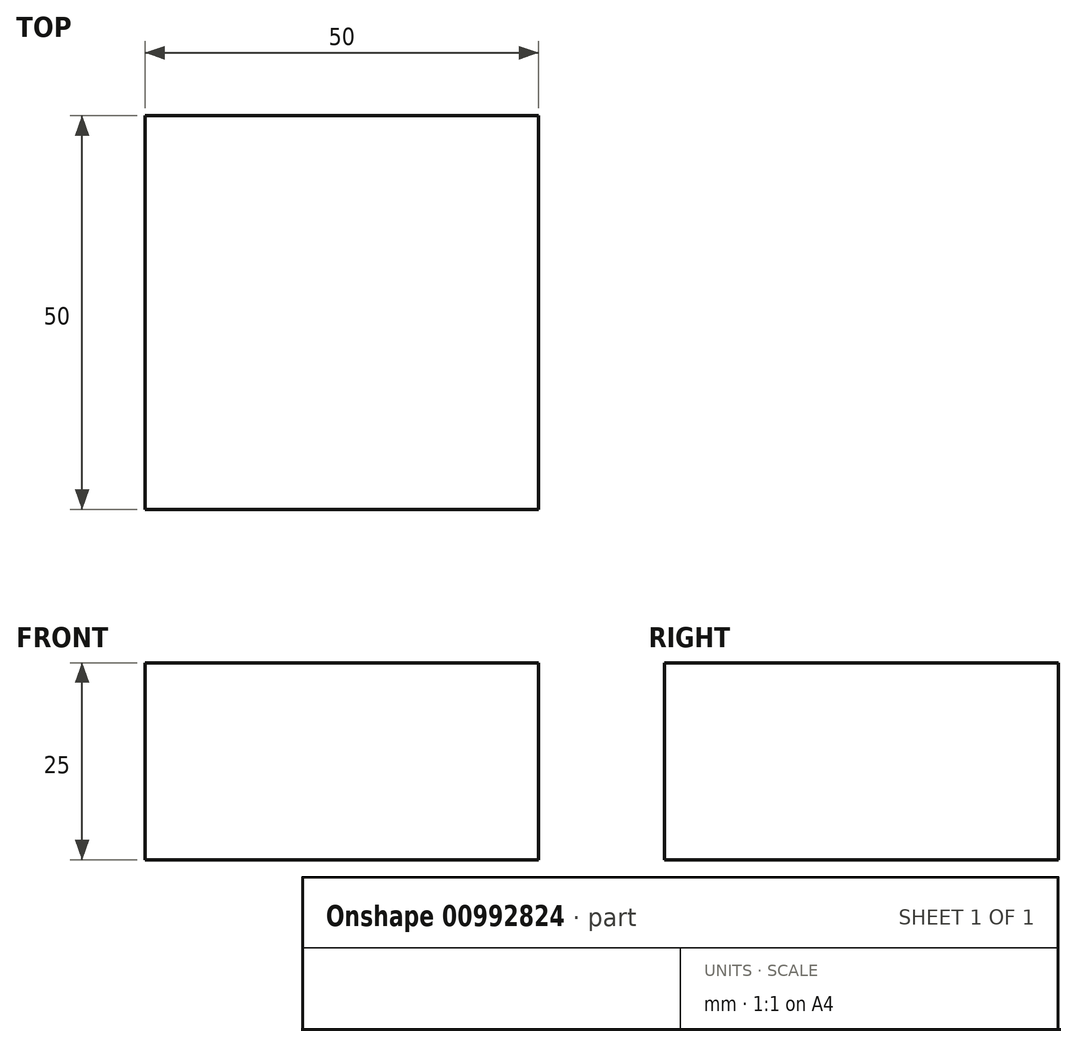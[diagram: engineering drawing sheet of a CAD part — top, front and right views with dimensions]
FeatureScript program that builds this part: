
annotation { "Feature Type Name" : "Feature", "Feature Type Description" : "" }
export const myFeature = defineFeature(function(context is Context, id is Id, definition is map)
    precondition{}
    {
        {
            var Q0;
            Q0=qCreatedBy(makeId("Top.planeOp"),FACE);
            var sketch = newSketch(context, id + "F0", { "sketchPlane" : qUnion([Q0])});
            skLineSegment(sketch, "E0.bottom", {"start": v(-31.6, 37.18) * mm, "end": v(18.4, 37.18) * mm});
            skLineSegment(sketch, "E0.top", {"start": v(-31.6, -12.82) * mm, "end": v(18.4, -12.82) * mm});
            skLineSegment(sketch, "E0.left", {"start": v(-31.6, 37.18) * mm, "end": v(-31.6, -12.82) * mm});
            skLineSegment(sketch, "E0.right", {"start": v(18.4, 37.18) * mm, "end": v(18.4, -12.82) * mm});
            skSolve(sketch);
        }
        {
            var Q0;
            Q0=makeQuery(id+"F0.imprint","IMPRINT",FACE,{"disambiguationData":[TD([[makeQuery(id+"F0.imprint","IMPRINT",EDGE,{"derivedFrom":sQuery(id+"F0.wireOp",EDGE,"E0.bottom")}),-1.0]])]});
            extrude(context, id + "F1", {"entities" : qUnion([Q0]), "depth" : 25 * mm, "offsetDistance" : 25 * mm});
        }
    });
